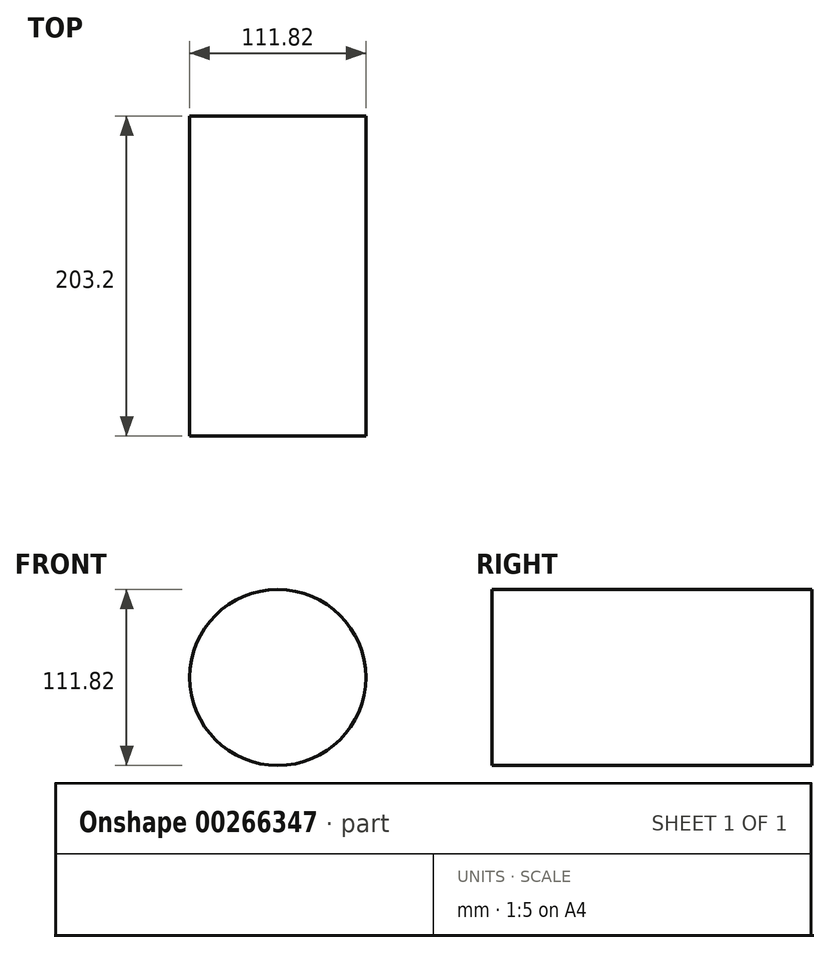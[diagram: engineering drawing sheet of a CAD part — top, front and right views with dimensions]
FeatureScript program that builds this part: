
annotation { "Feature Type Name" : "Feature", "Feature Type Description" : "" }
export const myFeature = defineFeature(function(context is Context, id is Id, definition is map)
    precondition{}
    {
        {
            var Q0;
            Q0=qCreatedBy(makeId("Front.planeOp"),FACE);
            var sketch = newSketch(context, id + "F0", { "sketchPlane" : qUnion([Q0])});
            skCircle(sketch, "E0", {"center": v(0, 0) * mm, "radius": 55.91 * mm});
            skSolve(sketch);
        }
        {
            var Q0;
            Q0 = qSketchRegion(id + "F0", true);
            extrude(context, id + "F1", {"entities" : qUnion([Q0]), "depth" : 203.2 * mm});
        }
    });
